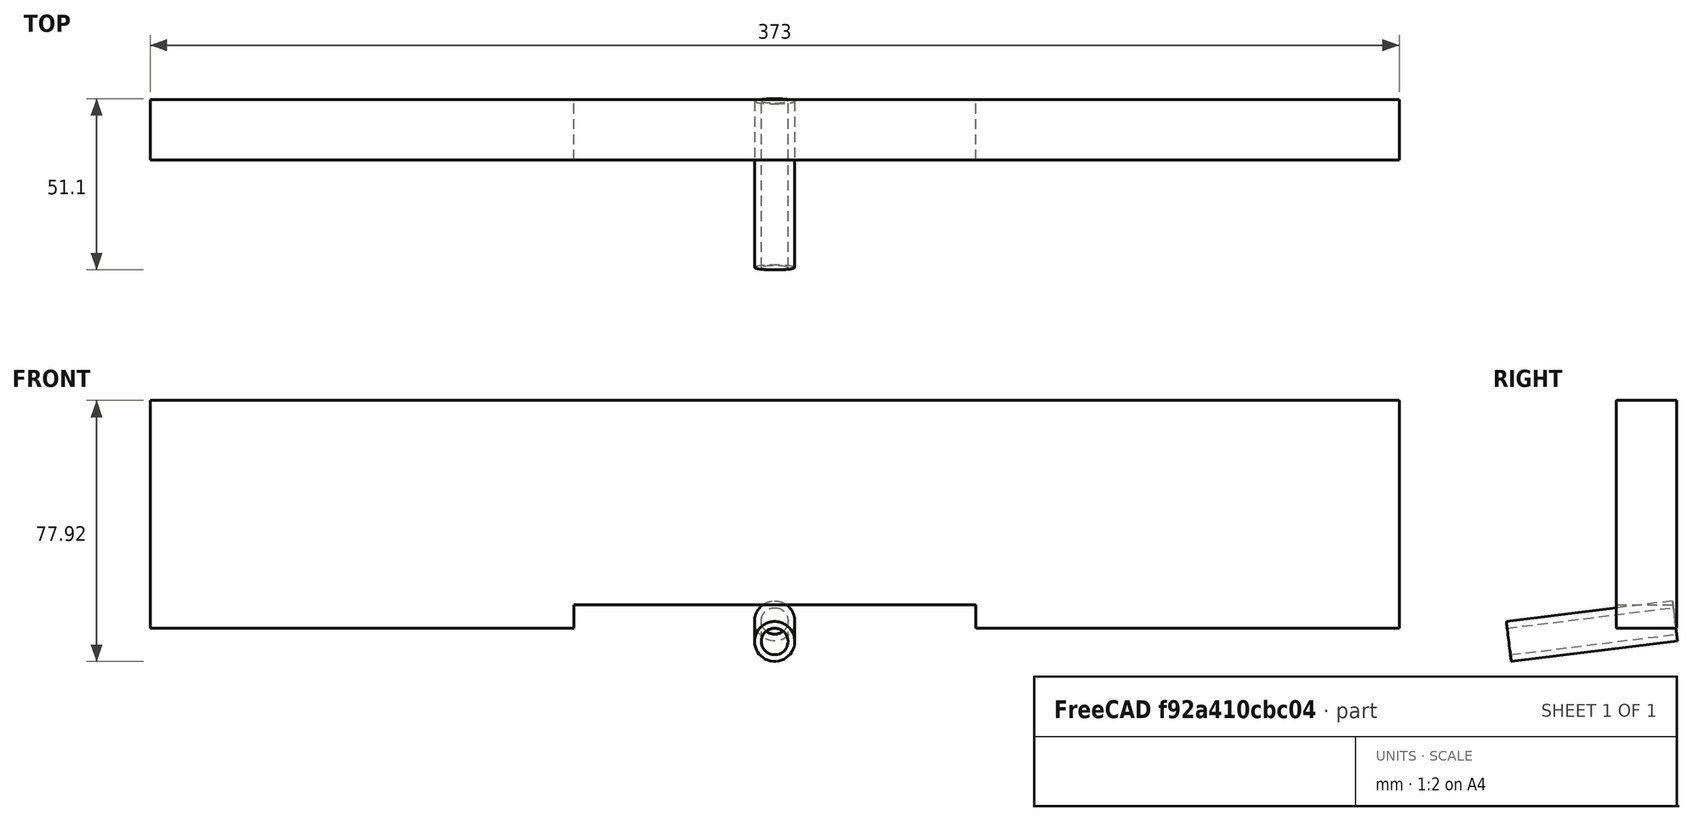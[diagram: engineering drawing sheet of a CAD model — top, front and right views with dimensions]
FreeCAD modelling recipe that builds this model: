
FCSTD DOCUMENT  (FreeCAD 0.19R)
Label: podnica_pokrovcek
License: All rights reserved
LicenseURL: http://en.wikipedia.org/wiki/All_rights_reserved
objects: App::Link×13, PartDesign::Line×12, TechDraw::DrawViewDimension×9, Sketcher::SketchObject×6, PartDesign::CoordinateSystem×6, TechDraw::DrawProjGroupItem×6, TechDraw::DrawRichAnno×5, App::Part×4, PartDesign::Body×3, App::DocumentObjectGroup×3, TechDraw::DrawProjGroup×3, PartDesign::Pad×2, TechDraw::DrawSVGTemplate×1, PartDesign::Pocket×1, App::FeaturePython×1, PartDesign::Revolution×1, TechDraw::DrawPage×1
note: 35 computed .brp shape members not serialized (recipe doc carries the construction recipe); baked Part::Feature solids carry a one-line shape summary decoded from their .brp

FEATURE [PartDesign::Body] Body
  Origin = -> Origin001
FEATURE [Sketcher::SketchObject] Sketch
  FullyConstrained = true
  MapMode = 5
  Placement = pos=(0,0,0) rot=(1,0,0;1.5708rad)
  Support = -> [XZ_Plane001]
  sketch-geometry (8):
    g0: LineSegment StartX=-186.5 StartY=0 StartZ=0 EndX=-186.5 EndY=68 EndZ=0
    g1: LineSegment StartX=-186.5 StartY=68 StartZ=0 EndX=186.5 EndY=68 EndZ=0
    g2: LineSegment StartX=186.5 StartY=68 StartZ=0 EndX=186.5 EndY=0 EndZ=0
    g3: LineSegment StartX=186.5 StartY=0 StartZ=0 EndX=60 EndY=0 EndZ=0
    g4: LineSegment StartX=60 StartY=0 StartZ=0 EndX=60 EndY=7 EndZ=0
    g5: LineSegment StartX=60 StartY=7 StartZ=0 EndX=-60 EndY=7 EndZ=0
    g6: LineSegment StartX=-60 StartY=7 StartZ=0 EndX=-60 EndY=0 EndZ=0
    g7: LineSegment StartX=-60 StartY=0 StartZ=0 EndX=-186.5 EndY=0 EndZ=0
  constraints (23):
    c: Vertical(g0)
    c: Coincident(g0,g1)
    c: Horizontal(g1)
    c: Coincident(g1,g2)
    c: Vertical(g2)
    c: Coincident(g2,g3)
    c: Horizontal(g3)
    c: Coincident(g3,g4)
    c: Vertical(g4)
    c: Coincident(g4,g5)
    c: Horizontal(g5)
    c: Coincident(g5,g6)
    c: Vertical(g6)
    c: Coincident(g6,g7)
    c: Coincident(g7,g0)
    c: Horizontal(g7)
    c: Symmetric(g6,g3,g-1)
    c: Horizontal(g6,g3)
    c: Equal(g7,g3)
    c: DistanceY(g4,g4) = 7  'H2'
    c: DistanceX(g5,g5) = 120  'L2'
    c: DistanceY(g0,g0) = 68  'H'
    c: DistanceX(g1,g1) = 373  'L'
FEATURE [PartDesign::Pad] Pad
  Direction = (1,1,1)
  Length = 18
  Length2 = 100
  Placement = pos=(0,0,0) rot=(1,0,0;1.5708rad)
  Profile = -> Sketch
  Reversed = true
  Type = 0
FEATURE [TechDraw::DrawSVGTemplate] Template
  EditableTexts = AVTOR=Brane Borštnik,AVTOR_2=Risal: Janez Paternoster,DATUM=6.5.2022,MATERIAL=Les, smreka,MERILO=1:2,NAZIV=Pokrovček v podnici,+3 more (map truncated)
  Height = 210
  Orientation = 1
  Width = 297
FEATURE [Sketcher::SketchObject] Sketch001
  FullyConstrained = true
  MapMode = 5
  Placement = pos=(0,0,0) rot=(1,0,0;1.5708rad)
  Support = -> [XZ_Plane001]
  sketch-geometry (23):
    g0: Circle CenterX=-165 CenterY=56 CenterZ=0 NormalX=0 NormalY=0 NormalZ=1 AngleXU=0 Radius=5.5
    g1: Circle CenterX=-135 CenterY=56 CenterZ=0 NormalX=0 NormalY=0 NormalZ=1 AngleXU=0 Radius=5.5
    g2: Circle CenterX=-105 CenterY=56 CenterZ=0 NormalX=0 NormalY=0 NormalZ=1 AngleXU=0 Radius=5.5
    g3: Circle CenterX=-75 CenterY=56 CenterZ=0 NormalX=0 NormalY=0 NormalZ=1 AngleXU=0 Radius=5.5
    g4: Circle CenterX=-45 CenterY=56 CenterZ=0 NormalX=0 NormalY=0 NormalZ=1 AngleXU=0 Radius=5.5
    g5: Circle CenterX=-15 CenterY=56 CenterZ=0 NormalX=0 NormalY=0 NormalZ=1 AngleXU=0 Radius=5.5
    g6: Circle CenterX=15 CenterY=56 CenterZ=0 NormalX=0 NormalY=0 NormalZ=1 AngleXU=0 Radius=5.5
    g7: Circle CenterX=45 CenterY=56 CenterZ=0 NormalX=0 NormalY=0 NormalZ=1 AngleXU=0 Radius=5.5
    g8: Circle CenterX=75 CenterY=56 CenterZ=0 NormalX=0 NormalY=0 NormalZ=1 AngleXU=0 Radius=5.5
    g9: Circle CenterX=105 CenterY=56 CenterZ=0 NormalX=0 NormalY=0 NormalZ=1 AngleXU=0 Radius=5.5
    g10: Circle CenterX=135 CenterY=56 CenterZ=0 NormalX=0 NormalY=0 NormalZ=1 AngleXU=0 Radius=5.5
    g11: Circle CenterX=165 CenterY=56 CenterZ=0 NormalX=0 NormalY=0 NormalZ=1 AngleXU=0 Radius=5.5
    g12: LineSegment StartX=-165 StartY=56 StartZ=0 EndX=-135 EndY=56 EndZ=0
    g13: LineSegment StartX=-135 StartY=56 StartZ=0 EndX=-105 EndY=56 EndZ=0
    g14: LineSegment StartX=-105 StartY=56 StartZ=0 EndX=-75 EndY=56 EndZ=0
    g15: LineSegment StartX=-75 StartY=56 StartZ=0 EndX=-45 EndY=56 EndZ=0
    g16: LineSegment StartX=-45 StartY=56 StartZ=0 EndX=-15 EndY=56 EndZ=0
    g17: LineSegment StartX=-15 StartY=56 StartZ=0 EndX=15 EndY=56 EndZ=0
    g18: LineSegment StartX=15 StartY=56 StartZ=0 EndX=45 EndY=56 EndZ=0
    g19: LineSegment StartX=45 StartY=56 StartZ=0 EndX=75 EndY=56 EndZ=0
    g20: LineSegment StartX=75 StartY=56 StartZ=0 EndX=105 EndY=56 EndZ=0
    g21: LineSegment StartX=105 StartY=56 StartZ=0 EndX=135 EndY=56 EndZ=0
    g22: LineSegment StartX=135 StartY=56 StartZ=0 EndX=165 EndY=56 EndZ=0
  constraints (50):
    c: Horizontal(g12)
    c: Coincident(g12,g13)
    c: Horizontal(g13)
    c: Coincident(g13,g14)
    c: Horizontal(g14)
    c: Coincident(g14,g15)
    c: Coincident(g15,g16)
    c: Horizontal(g16)
    c: Coincident(g16,g17)
    c: Coincident(g17,g18)
    c: Horizontal(g18)
    c: Coincident(g18,g19)
    c: Horizontal(g19)
    c: Coincident(g19,g20)
    c: Horizontal(g20)
    c: Coincident(g20,g21)
    c: Horizontal(g21)
    c: Coincident(g21,g22)
    c: Horizontal(g22)
    c: Horizontal(g15)
    c: Symmetric(g16,g17,g-2)
    c: Equal(g17,g16)
    c: Equal(g17,g15)
    c: Equal(g17,g14)
    c: Equal(g17,g13)
    c: Equal(g17,g12)
    c: Equal(g17, g18-g22) x5
    c: Coincident(g0,g12)
    c: Coincident(g1,g12)
    c: Coincident(g2,g13)
    c: Coincident(g3,g14)
    c: Coincident(g4,g15)
    c: Coincident(g5,g16)
    c: Coincident(g6,g17)
    c: Coincident(g18,g7)
    c: Coincident(g8,g19)
    c: Coincident(g9,g20)
    c: Coincident(g22,g11)
    c: Coincident(g10,g21)
    c: Equal(g5,g4)
    c: Equal(g5,g3)
    c: Equal(g5,g2)
    c: Equal(g5,g1)
    c: Equal(g5,g0)
    c: Equal(g5,g6)
    c: Equal(g6, g7-g11) x5
    c: Diameter(g0) = 11
    c: DistanceX(g17,g17) = 30
    c: DistanceX(g0,g11) = 330
    c: DistanceY(g-1,g0) = 56
FEATURE [PartDesign::Pocket] Pocket
  BaseFeature = -> Pad
  Length = 5
  Length2 = 100
  Placement = pos=(0,0,0) rot=(1,0,0;1.5708rad)
  Profile = -> Sketch001
  Type = 1
FEATURE [PartDesign::CoordinateSystem] LCS_Origin
  AttacherType = Attacher::AttachEngine3D
  MapMode = 2
  Support = -> [X_Axis002]
FEATURE [App::FeaturePython] Variables  # WARN: FeaturePython — macro-defined, semantics opaque (R4)
  Type = App::PropertyContainer
FEATURE [App::DocumentObjectGroup] Constraints
FEATURE [App::DocumentObjectGroup] Configurations
FEATURE [PartDesign::CoordinateSystem] LCS_0
  AttacherType = Attacher::AttachEngine3D
  MapMode = 2
  Support = -> [X_Axis003]
FEATURE [PartDesign::CoordinateSystem] LCS_0001
  AttacherType = Attacher::AttachEngine3D
  MapMode = 2
  Support = -> [X_Axis004]
FEATURE [Sketcher::SketchObject] Sketch004
  FullyConstrained = true
  MapMode = 5
  Placement = pos=(0,0,0) rot=(1,0,0;1.5708rad)
  Support = -> [XZ_Plane004]
  expr: Constraints[18] = Sketch.Constraints.L
  expr: Constraints[19] = Sketch.Constraints.H
  expr: Constraints[20] = Sketch.Constraints.L2
  expr: Constraints[21] = Sketch.Constraints.H2
  sketch-geometry (8):
    g0: LineSegment StartX=-186.5 StartY=68 StartZ=0 EndX=186.5 EndY=68 EndZ=0
    g1: LineSegment StartX=186.5 StartY=68 StartZ=0 EndX=186.5 EndY=0 EndZ=0
    g2: LineSegment StartX=186.5 StartY=0 StartZ=0 EndX=60 EndY=0 EndZ=0
    g3: LineSegment StartX=60 StartY=0 StartZ=0 EndX=60 EndY=7 EndZ=0
    g4: LineSegment StartX=60 StartY=7 StartZ=0 EndX=-60 EndY=7 EndZ=0
    g5: LineSegment StartX=-60 StartY=7 StartZ=0 EndX=-60 EndY=0 EndZ=0
    g6: LineSegment StartX=-60 StartY=0 StartZ=0 EndX=-186.5 EndY=0 EndZ=0
    g7: LineSegment StartX=-186.5 StartY=0 StartZ=0 EndX=-186.5 EndY=68 EndZ=0
  constraints (23):
    c: Horizontal(g0)
    c: Coincident(g0,g1)
    c: Vertical(g1)
    c: Coincident(g1,g2)
    c: Horizontal(g2)
    c: Coincident(g2,g3)
    c: Vertical(g3)
    c: Coincident(g3,g4)
    c: Horizontal(g4)
    c: Coincident(g4,g5)
    c: Vertical(g5)
    c: Coincident(g5,g6)
    c: Horizontal(g6)
    c: Coincident(g6,g7)
    c: Coincident(g7,g0)
    c: Vertical(g7)
    c: Horizontal(g5,g2)
    c: Symmetric(g2,g5,g-1)
    c: DistanceX(g0,g0) = 373
    c: DistanceY(g7,g7) = 68
    c: DistanceX(g4,g4) = 120
    c: DistanceY(g5,g5) = 7
    c: Equal(g6,g2)
FEATURE [PartDesign::Pad] Pad001
  Direction = (1,1,1)
  Length = 18
  Length2 = 100
  Placement = pos=(0,0,0) rot=(1,0,0;1.5708rad)
  Profile = -> Sketch004
  Reversed = true
  Type = 0
  expr: Length = Pad.Length
FEATURE [Sketcher::SketchObject] Sketch005
  FullyConstrained = true
  MapMode = 5
  Placement = pos=(0,0,0) rot=(0.57735,0.57735,0.57735;2.0944rad)
  Support = -> [YZ_Plane004]
  sketch-geometry (4):
    g0: LineSegment StartX=-32.6227 StartY=0 StartZ=0 EndX=17 EndY=6.1307 EndZ=0
    g1: LineSegment StartX=17 StartY=6.1307 StartZ=0 EndX=16.7548 EndY=8.11561 EndZ=0
    g2: LineSegment StartX=16.7548 StartY=8.11561 StartZ=0 EndX=-32.868 EndY=1.98491 EndZ=0
    g3: LineSegment StartX=-32.868 StartY=1.98491 StartZ=0 EndX=-32.6227 EndY=0 EndZ=0
  constraints (12):
    c: Coincident(g0,g1)
    c: Coincident(g1,g2)
    c: Coincident(g2,g3)
    c: Coincident(g3,g0)
    c: Perpendicular(g1,g0)
    c: Perpendicular(g2,g1)
    c: Perpendicular(g3,g2)
    c: Distance(g-1,g0) = 4
    c: Distance(g-1,g2) = 6
    c: DistanceX(g-1,g0) = 17
    c: Distance(g2) = 50
    c: Horizontal(g0,g-1)
FEATURE [PartDesign::Body] Body_2
  Group = -> [LCS_0001,Sketch004,Pad001,Sketch005]
  Origin = -> Origin004
  Tip = -> Pad001
FEATURE [App::Part] pokrovcek_navaden
  Group = -> [LCS_0,Body_2]
  Origin = -> Origin003
FEATURE [PartDesign::CoordinateSystem] LCS_0002
  AttacherType = Attacher::AttachEngine3D
  MapMode = 2
  Support = -> [X_Axis005]
FEATURE [PartDesign::CoordinateSystem] LCS_0003
  AttacherType = Attacher::AttachEngine3D
  MapMode = 2
  Support = -> [X_Axis006]
FEATURE [Sketcher::SketchObject] Sketch006
  FullyConstrained = true
  MapMode = 5
  Placement = pos=(0,0,0) rot=(0.57735,0.57735,0.57735;2.0944rad)
  Support = -> [YZ_Plane006]
  sketch-geometry (5):
    g0: LineSegment StartX=-32.6227 StartY=0 StartZ=0 EndX=17 EndY=6.1307 EndZ=0
    g1: LineSegment StartX=17 StartY=6.1307 StartZ=0 EndX=16.7548 EndY=8.11561 EndZ=0
    g2: LineSegment StartX=16.7548 StartY=8.11561 StartZ=0 EndX=-32.868 EndY=1.98491 EndZ=0
    g3: LineSegment StartX=-32.868 StartY=1.98491 StartZ=0 EndX=-32.6227 EndY=0 EndZ=0
    g4: LineSegment StartX=-32.6227 StartY=-4.03041 StartZ=0 EndX=17 EndY=2.10028 EndZ=0
  constraints (16):
    c: Coincident(g0,g1)
    c: Coincident(g1,g2)
    c: Coincident(g2,g3)
    c: Coincident(g3,g0)
    c: Perpendicular(g1,g0)
    c: Perpendicular(g2,g1)
    c: Perpendicular(g3,g2)
    c: Distance(g-1,g0) = 4
    c: Distance(g-1,g2) = 6
    c: DistanceX(g-1,g0) = 17
    c: Distance(g2) = 50
    c: Horizontal(g0,g-1)
    c: PointOnObject(g-1,g4)
    c: Parallel(g4,g0)
    c: Vertical(g0,g4)
    c: Vertical(g0,g4)
FEATURE [PartDesign::Revolution] Revolution
  Angle = 360
  Axis = (1.52e-14,49.6227,6.1307)
  Base = (-1e-14,-32.6227,-4.03041)
  Placement = pos=(0,0,0) rot=(0.57735,0.57735,0.57735;2.0944rad)
  Profile = -> Sketch006
  ReferenceAxis = -> Sketch006 [Axis0]
FEATURE [App::Link] pokrovcek_smukalnik  label="pokrovcek_smukalnik001"
  AssemblyType = Part::Link
  LinkedObject = -> Part
FEATURE [PartDesign::CoordinateSystem] LCS_1
  AttacherType = Attacher::AttachEngine3D
FEATURE [PartDesign::Line] HoleAxis_1
  AttacherType = Attacher::AttachEngineLine
  Length = 15.4997
  MapMode = 19
  Placement = pos=(-165,1.24e-14,56) rot=(1,0,0;1.5708rad)
  ResizeMode = 1
  Support = -> [Pocket]
FEATURE [App::Link] cevka002  label="cevka1"
  AssemblyType = Part::Link
  AttachedBy = #LCS_0002
  AttachedTo = pokrovcek_smukalnik#HoleAxis_1
  AttachmentOffset = pos=(0,0,0) rot=(1,0,0;4.71239rad)
  LinkPlacement = pos=(-165,3.73e-14,56) rot=(0,0,1;0rad)
  LinkedObject = -> cevka
  Placement = pos=(-165,3.73e-14,56) rot=(0,0,1;0rad)
  SolverId = Asm4EE
  expr: Placement = pokrovcek_smukalnik.Placement * HoleAxis_1.Placement * AttachmentOffset * LCS_0002.Placement ^ -1
FEATURE [PartDesign::Line] HoleAxis_2 .. HoleAxis_12  x11 (patterned run collapsed; names and placements below)
  AttacherType = Attacher::AttachEngineLine
  Length = 15.4997
  MapMode = 19
  ResizeMode = 1
  Support = -> [Pocket]
  placements: 11 in arithmetic series — first pos=(-135,1.24e-14,56) rot=(1,0,0;1.5708rad), step (30,0,0), last pos=(165,1.24e-14,56) rot=(1,0,0;1.5708rad)
FEATURE [App::Part] Part  label="pokrovcek_smukalnik"
  Group = -> [Body,LCS_1,Sketch001,Pocket,Pad,Sketch,HoleAxis_1,HoleAxis_2,HoleAxis_3,HoleAxis_4,HoleAxis_5,HoleAxis_6,HoleAxis_7,HoleAxis_8,HoleAxis_9,HoleAxis_10,HoleAxis_11,HoleAxis_12]
  Origin = -> Origin
FEATURE [TechDraw::DrawProjGroupItem] ProjItem  label="Front"
  CoarseView = false
  Direction = (0,-1,0)
  Focus = 100
  HardHidden = false
  IsoCount = 0
  IsoHidden = false
  IsoVisible = false
  LockPosition = true
  Perspective = false
  Rotation = 0
  RotationVector = (1,0,0)
  Scale = 0.5
  ScaleType = 2
  SeamHidden = false
  SeamVisible = true
  SmoothHidden = false
  SmoothVisible = true
  Source = -> [Part]
  Type = 0
  X = 0
  XDirection = (1,0,0)
  Y = 0
FEATURE [TechDraw::DrawProjGroupItem] ProjItem001  label="Left"
  CoarseView = false
  Direction = (-1,-1e-16,0)
  Focus = 100
  HardHidden = false
  IsoCount = 0
  IsoHidden = false
  IsoVisible = false
  LockPosition = false
  Perspective = false
  Rotation = 0
  RotationVector = (1,0,0)
  Scale = 0.5
  ScaleType = 2
  SeamHidden = false
  SeamVisible = true
  SmoothHidden = false
  SmoothVisible = true
  Source = -> [Part]
  Type = 1
  X = 127.75
  XDirection = (1e-16,-1,0)
  Y = 0
FEATURE [TechDraw::DrawProjGroup] ProjGroup
  Anchor = -> ProjItem
  AutoDistribute = true
  LockPosition = false
  ProjectionType = 0
  Rotation = 0
  Scale = 0.5
  ScaleType = 0
  Source = -> [Part]
  Views = -> [ProjItem,ProjItem001]
  X = 113.771
  Y = 141.789
  spacingX = 30
  spacingY = 15
FEATURE [TechDraw::DrawViewDimension] Dimension
  Arbitrary = false
  ArbitraryTolerances = false
  EqualTolerance = true
  FormatSpec = %.6g
  FormatSpecOverTolerance = %+.6g
  FormatSpecUnderTolerance = %+.6g
  Inverted = false
  LockPosition = false
  MeasureType = 1
  OverTolerance = 0
  References2D = -> [ProjItem001]
  Rotation = 0
  Scale = 0.5
  ScaleType = 0
  TheoreticalExact = false
  Type = 1
  UnderTolerance = 0
  X = -0.601719
  Y = 39.2636
FEATURE [TechDraw::DrawViewDimension] Dimension001
  Arbitrary = false
  ArbitraryTolerances = false
  EqualTolerance = true
  FormatSpec = %.6g
  FormatSpecOverTolerance = %+.6g
  FormatSpecUnderTolerance = %+.6g
  Inverted = false
  LockPosition = false
  MeasureType = 1
  OverTolerance = 0
  References2D = -> [ProjItem001]
  Rotation = 0
  Scale = 0.5
  ScaleType = 0
  TheoreticalExact = false
  Type = 2
  UnderTolerance = 0
  X = 16.2335
  Y = 1.80516
FEATURE [TechDraw::DrawViewDimension] Dimension002
  Arbitrary = false
  ArbitraryTolerances = false
  EqualTolerance = true
  FormatSpec = %.6g
  FormatSpecOverTolerance = %+.6g
  FormatSpecUnderTolerance = %+.6g
  Inverted = false
  LockPosition = false
  MeasureType = 1
  OverTolerance = 0
  References2D = -> [ProjItem]
  Rotation = 0
  Scale = 0.5
  ScaleType = 0
  TheoreticalExact = false
  Type = 1
  UnderTolerance = 0
  X = 0.902579
  Y = 42.5731
FEATURE [TechDraw::DrawViewDimension] Dimension003
  Arbitrary = false
  ArbitraryTolerances = false
  EqualTolerance = true
  FormatSpec = %.6g
  FormatSpecOverTolerance = %+.6g
  FormatSpecUnderTolerance = %+.6g
  Inverted = false
  LockPosition = false
  MeasureType = 1
  OverTolerance = 0
  References2D = -> [ProjItem]
  Rotation = 0
  Scale = 0.5
  ScaleType = 0
  TheoreticalExact = false
  Type = 1
  UnderTolerance = 0
  X = -2.10602
  Y = -25.8352
FEATURE [TechDraw::DrawViewDimension] Dimension004
  Arbitrary = false
  ArbitraryTolerances = false
  EqualTolerance = true
  FormatSpec = %.6g
  FormatSpecOverTolerance = %+.6g
  FormatSpecUnderTolerance = %+.6g
  Inverted = false
  LockPosition = false
  MeasureType = 1
  OverTolerance = 0
  References2D = -> [ProjItem]
  Rotation = 0
  Scale = 0.5
  ScaleType = 0
  TheoreticalExact = false
  Type = 2
  UnderTolerance = 0
  X = -36.6189
  Y = -27.5852
FEATURE [TechDraw::DrawViewDimension] Dimension005
  Arbitrary = false
  ArbitraryTolerances = false
  EqualTolerance = true
  FormatSpec = %.6g
  FormatSpecOverTolerance = %+.6g
  FormatSpecUnderTolerance = %+.6g
  Inverted = false
  LockPosition = false
  MeasureType = 1
  OverTolerance = 0
  References2D = -> [ProjItem]
  Rotation = 0
  Scale = 0.5
  ScaleType = 0
  TheoreticalExact = false
  Type = 1
  UnderTolerance = 0
  X = -0.30086
  Y = 34.1662
FEATURE [TechDraw::DrawViewDimension] Dimension006
  Arbitrary = false
  ArbitraryTolerances = false
  EqualTolerance = true
  FormatSpec = ⌀%.6g, 12x
  FormatSpecOverTolerance = %+.6g
  FormatSpecUnderTolerance = %+.6g
  Inverted = false
  LockPosition = false
  MeasureType = 1
  OverTolerance = 0
  References2D = -> [ProjItem]
  Rotation = 0
  Scale = 0.5
  ScaleType = 0
  TheoreticalExact = false
  Type = 5
  UnderTolerance = 0
  X = -75.5158
  Y = 28.5817
FEATURE [App::Link] cevka003
  AssemblyType = Part::Link
  AttachedBy = #LCS_0002
  AttachedTo = pokrovcek_smukalnik#HoleAxis_2
  AttachmentOffset = pos=(0,0,0) rot=(1,0,0;4.71239rad)
  LinkPlacement = pos=(-135,3.73e-14,56) rot=(0,0,1;0rad)
  LinkedObject = -> cevka
  Placement = pos=(-135,3.73e-14,56) rot=(0,0,1;0rad)
  SolverId = Asm4EE
  expr: Placement = pokrovcek_smukalnik.Placement * HoleAxis_2.Placement * AttachmentOffset * LCS_0002.Placement ^ -1
FEATURE [App::Link] cevka_2
  AssemblyType = Part::Link
  AttachedBy = #LCS_0002
  AttachedTo = pokrovcek_smukalnik#HoleAxis_3
  AttachmentOffset = pos=(0,0,0) rot=(1,0,0;4.71239rad)
  LinkPlacement = pos=(-105,3.73e-14,56) rot=(0,0,1;0rad)
  LinkedObject = -> cevka
  Placement = pos=(-105,3.73e-14,56) rot=(0,0,1;0rad)
  SolverId = Asm4EE
  expr: Placement = pokrovcek_smukalnik.Placement * HoleAxis_3.Placement * AttachmentOffset * LCS_0002.Placement ^ -1
FEATURE [App::Link] cevka_3
  AssemblyType = Part::Link
  AttachedBy = #LCS_0002
  AttachedTo = pokrovcek_smukalnik#HoleAxis_4
  AttachmentOffset = pos=(0,0,0) rot=(1,0,0;4.71239rad)
  LinkPlacement = pos=(-75,3.73e-14,56) rot=(0,0,1;0rad)
  LinkedObject = -> cevka
  Placement = pos=(-75,3.73e-14,56) rot=(0,0,1;0rad)
  SolverId = Asm4EE
  expr: Placement = pokrovcek_smukalnik.Placement * HoleAxis_4.Placement * AttachmentOffset * LCS_0002.Placement ^ -1
FEATURE [App::Link] cevka_4
  AssemblyType = Part::Link
  AttachedBy = #LCS_0002
  AttachedTo = pokrovcek_smukalnik#HoleAxis_5
  AttachmentOffset = pos=(0,0,0) rot=(1,0,0;4.71239rad)
  LinkPlacement = pos=(-45,3.73e-14,56) rot=(0,0,1;0rad)
  LinkedObject = -> cevka
  Placement = pos=(-45,3.73e-14,56) rot=(0,0,1;0rad)
  SolverId = Asm4EE
  expr: Placement = pokrovcek_smukalnik.Placement * HoleAxis_5.Placement * AttachmentOffset * LCS_0002.Placement ^ -1
FEATURE [App::Link] cevka_5
  AssemblyType = Part::Link
  AttachedBy = #LCS_0002
  AttachedTo = pokrovcek_smukalnik#HoleAxis_6
  AttachmentOffset = pos=(0,0,0) rot=(1,0,0;4.71239rad)
  LinkPlacement = pos=(-15,3.73e-14,56) rot=(0,0,1;0rad)
  LinkedObject = -> cevka
  Placement = pos=(-15,3.73e-14,56) rot=(0,0,1;0rad)
  SolverId = Asm4EE
  expr: Placement = pokrovcek_smukalnik.Placement * HoleAxis_6.Placement * AttachmentOffset * LCS_0002.Placement ^ -1
FEATURE [App::Link] cevka_6
  AssemblyType = Part::Link
  AttachedBy = #LCS_0002
  AttachedTo = pokrovcek_smukalnik#HoleAxis_7
  AttachmentOffset = pos=(0,0,0) rot=(1,0,0;4.71239rad)
  LinkPlacement = pos=(15,3.73e-14,56) rot=(0,0,1;0rad)
  LinkedObject = -> cevka
  Placement = pos=(15,3.73e-14,56) rot=(0,0,1;0rad)
  SolverId = Asm4EE
  expr: Placement = pokrovcek_smukalnik.Placement * HoleAxis_7.Placement * AttachmentOffset * LCS_0002.Placement ^ -1
FEATURE [App::Link] cevka_7
  AssemblyType = Part::Link
  AttachedBy = #LCS_0002
  AttachedTo = pokrovcek_smukalnik#HoleAxis_8
  AttachmentOffset = pos=(0,0,0) rot=(1,0,0;4.71239rad)
  LinkPlacement = pos=(45,3.73e-14,56) rot=(0,0,1;0rad)
  LinkedObject = -> cevka
  Placement = pos=(45,3.73e-14,56) rot=(0,0,1;0rad)
  SolverId = Asm4EE
  expr: Placement = pokrovcek_smukalnik.Placement * HoleAxis_8.Placement * AttachmentOffset * LCS_0002.Placement ^ -1
FEATURE [App::Link] cevka_8
  AssemblyType = Part::Link
  AttachedBy = #LCS_0002
  AttachedTo = pokrovcek_smukalnik#HoleAxis_9
  AttachmentOffset = pos=(0,0,0) rot=(1,0,0;4.71239rad)
  LinkPlacement = pos=(75,3.73e-14,56) rot=(0,0,1;0rad)
  LinkedObject = -> cevka
  Placement = pos=(75,3.73e-14,56) rot=(0,0,1;0rad)
  SolverId = Asm4EE
  expr: Placement = pokrovcek_smukalnik.Placement * HoleAxis_9.Placement * AttachmentOffset * LCS_0002.Placement ^ -1
FEATURE [App::Link] cevka_9
  AssemblyType = Part::Link
  AttachedBy = #LCS_0002
  AttachedTo = pokrovcek_smukalnik#HoleAxis_10
  AttachmentOffset = pos=(0,0,0) rot=(1,0,0;4.71239rad)
  LinkPlacement = pos=(105,3.73e-14,56) rot=(0,0,1;0rad)
  LinkedObject = -> cevka
  Placement = pos=(105,3.73e-14,56) rot=(0,0,1;0rad)
  SolverId = Asm4EE
  expr: Placement = pokrovcek_smukalnik.Placement * HoleAxis_10.Placement * AttachmentOffset * LCS_0002.Placement ^ -1
FEATURE [App::Link] cevka_10
  AssemblyType = Part::Link
  AttachedBy = #LCS_0002
  AttachedTo = pokrovcek_smukalnik#HoleAxis_11
  AttachmentOffset = pos=(0,0,0) rot=(1,0,0;4.71239rad)
  LinkPlacement = pos=(135,3.73e-14,56) rot=(0,0,1;0rad)
  LinkedObject = -> cevka
  Placement = pos=(135,3.73e-14,56) rot=(0,0,1;0rad)
  SolverId = Asm4EE
  expr: Placement = pokrovcek_smukalnik.Placement * HoleAxis_11.Placement * AttachmentOffset * LCS_0002.Placement ^ -1
FEATURE [App::Link] cevka_11
  AssemblyType = Part::Link
  AttachedBy = #LCS_0002
  AttachedTo = pokrovcek_smukalnik#HoleAxis_12
  AttachmentOffset = pos=(0,0,0) rot=(1,0,0;4.71239rad)
  LinkPlacement = pos=(165,3.73e-14,56) rot=(0,0,1;0rad)
  LinkedObject = -> cevka
  Placement = pos=(165,3.73e-14,56) rot=(0,0,1;0rad)
  SolverId = Asm4EE
  expr: Placement = pokrovcek_smukalnik.Placement * HoleAxis_12.Placement * AttachmentOffset * LCS_0002.Placement ^ -1
FEATURE [App::Part] Assembly
  AssemblyType = Part::Link
  Group = -> [LCS_Origin,Variables,Constraints,Configurations,pokrovcek_smukalnik,cevka002,cevka003,cevka_2,cevka_3,cevka_4,cevka_5,cevka_6,cevka_7,cevka_8,cevka_9,cevka_10,cevka_11]
  Origin = -> Origin002
  Type = Assembly
FEATURE [TechDraw::DrawProjGroupItem] ProjItem002  label="Front001"
  CoarseView = false
  Direction = (0,-1,0)
  Focus = 100
  HardHidden = false
  IsoCount = 0
  IsoHidden = false
  IsoVisible = false
  LockPosition = true
  Perspective = false
  Rotation = 0
  RotationVector = (1,0,0)
  ScaleType = 2
  SeamHidden = false
  SeamVisible = true
  SmoothHidden = false
  SmoothVisible = true
  Source = -> [pokrovcek_navaden]
  Type = 0
  X = 0
  XDirection = (1,0,0)
  Y = 0
FEATURE [TechDraw::DrawProjGroupItem] ProjItem003  label="Left001"
  CoarseView = false
  Direction = (-1,-1e-16,0)
  Focus = 100
  HardHidden = false
  IsoCount = 0
  IsoHidden = false
  IsoVisible = false
  LockPosition = false
  Perspective = false
  Rotation = 0
  RotationVector = (1,0,0)
  ScaleType = 2
  SeamHidden = false
  SeamVisible = true
  SmoothHidden = false
  SmoothVisible = true
  Source = -> [pokrovcek_navaden]
  Type = 1
  X = 112.75
  XDirection = (1e-16,-1,0)
  Y = 0
FEATURE [TechDraw::DrawProjGroup] ProjGroup001
  Anchor = -> ProjItem002
  AutoDistribute = true
  LockPosition = false
  ProjectionType = 0
  Rotation = 0
  Scale = 0.5
  ScaleType = 0
  Source = -> [pokrovcek_navaden]
  Views = -> [ProjItem002,ProjItem003]
  X = 114.804
  Y = 54.1547
  spacingX = 15
  spacingY = 15
FEATURE [Sketcher::SketchObject] Sketch007
  FullyConstrained = true
  MapMode = 5
  Placement = pos=(-9.1e-15,-32.1323,-3.96982) rot=(0.599592,0.599592,-0.530074;2.16676rad)
  Support = -> [Revolution]
FEATURE [PartDesign::Body] Body_3
  Group = -> [LCS_0003,Sketch006,Revolution,Sketch007]
  Origin = -> Origin006
  Tip = -> Revolution
FEATURE [App::Part] cevka
  Group = -> [LCS_0002,Body_3]
  Origin = -> Origin005
FEATURE [App::DocumentObjectGroup] Parts
  Group = -> [Part,pokrovcek_navaden,cevka]
FEATURE [TechDraw::DrawProjGroupItem] ProjItem007  label="Front004"
  CoarseView = false
  Direction = (0.997,-0.013,0.071)
  Focus = 100
  HardHidden = false
  IsoCount = 0
  IsoHidden = false
  IsoVisible = false
  LockPosition = true
  Perspective = false
  Rotation = 0
  RotationVector = (0.004,0.992,0.126)
  ScaleType = 2
  SeamHidden = false
  SeamVisible = true
  SmoothHidden = false
  SmoothVisible = true
  Source = -> [cevka]
  Type = 0
  X = 0
  XDirection = (0.004,0.992,0.126)
  Y = 0
FEATURE [TechDraw::DrawProjGroupItem] ProjItem008  label="Left002"
  CoarseView = false
  Direction = (-0.00396217,-0.992022,-0.126)
  Focus = 100
  HardHidden = false
  IsoCount = 0
  IsoHidden = false
  IsoVisible = false
  LockPosition = false
  Perspective = false
  Rotation = 0
  RotationVector = (1,0,0)
  ScaleType = 2
  SeamHidden = false
  SeamVisible = true
  SmoothHidden = false
  SmoothVisible = true
  Source = -> [cevka]
  Type = 1
  X = 30.568
  XDirection = (0.99739,-0.0130051,0.0710277)
  Y = 0
FEATURE [TechDraw::DrawProjGroup] ProjGroup004
  Anchor = -> ProjItem007
  AutoDistribute = true
  LockPosition = false
  ProjectionType = 0
  Rotation = 0
  Scale = 0.5
  ScaleType = 0
  Source = -> [cevka]
  Views = -> [ProjItem007,ProjItem008]
  X = 212.552
  Y = 95.1458
  spacingX = 15
  spacingY = 15
FEATURE [TechDraw::DrawViewDimension] Dimension009
  Arbitrary = false
  ArbitraryTolerances = false
  EqualTolerance = true
  FormatSpec = %.0f
  FormatSpecOverTolerance = %+.6g
  FormatSpecUnderTolerance = %+.6g
  Inverted = false
  LockPosition = false
  MeasureType = 1
  OverTolerance = 0
  References2D = -> [ProjItem007]
  Rotation = 0
  Scale = 0.5
  ScaleType = 0
  TheoreticalExact = false
  Type = 1
  UnderTolerance = 0
  X = 0.645995
  Y = 15.0715
FEATURE [TechDraw::DrawViewDimension] Dimension010
  Arbitrary = false
  ArbitraryTolerances = false
  EqualTolerance = true
  FormatSpec = ⌀%.0f
  FormatSpecOverTolerance = %+.6g
  FormatSpecUnderTolerance = %+.6g
  Inverted = false
  LockPosition = false
  MeasureType = 1
  OverTolerance = 0
  References2D = -> [ProjItem008]
  Rotation = 0
  Scale = 0.5
  ScaleType = 0
  TheoreticalExact = false
  Type = 5
  UnderTolerance = 0
  X = 13.033
  Y = 14.9402
FEATURE [TechDraw::DrawRichAnno] RichTextAnnotation
  AnnoParent = -> ProjItem007
  AnnoText = <!DOCTYPE HTML PUBLIC "-//W3C//DTD HTML 4.0//EN" "http://www.w3.org/TR/REC-html40/strict.dtd">\n<html><head><meta name="qrichtext" content="1" /><style type="text/css">\np, li { white-space: pre-wrap; }\n</style></head><body style=" font-family:'Ubuntu'; font-size:11pt; font-weight:400; font-style:normal;">\n<p style=" margin-top:0px; margin-bottom:0px; margin-left:0px; margin-right:0px; -qt-block-indent:0; text-indent:0px;"><span style=" font-size:10pt;">Cevke, 12 kom</span></p></body></html>
  LockPosition = false
  MaxWidth = -1
  Rotation = 0
  Scale = 0.5
  ScaleType = 0
  ShowFrame = false
  X = 19.8673
  Y = -10.8078
FEATURE [TechDraw::DrawRichAnno] RichTextAnnotation001
  AnnoParent = -> ProjItem
  AnnoText = <!DOCTYPE HTML PUBLIC "-//W3C//DTD HTML 4.0//EN" "http://www.w3.org/TR/REC-html40/strict.dtd">\n<html><head><meta name="qrichtext" content="1" /><style type="text/css">\np, li { white-space: pre-wrap; }\n</style></head><body style=" font-family:'Ubuntu'; font-size:11pt; font-weight:400; font-style:normal;">\n<p style=" margin-top:0px; margin-bottom:0px; margin-left:0px; margin-right:0px; -qt-block-indent:0; text-indent:0px;"><span style=" font-size:10pt;">Pokrovček za smukalnik.</span></p>\n<p style=" margin-top:0px; margin-bottom:0px; margin-left:0px; margin-right:0px; -qt-block-indent:0; text-indent:0px;"><span style=" font-size:10pt;">V luknje se vstavijo cevke,</span></p>\n<p style=" margin-top:0px; margin-bottom:0px; margin-left:0px; margin-right:0px; -qt-block-indent:0; text-indent:0px;"><span style=" font-size:10pt;">ki naj bodo obrnjene rahlo navzdol</span></p></body></html>
  LockPosition = false
  MaxWidth = -1
  Rotation = 0
  Scale = 0.5
  ScaleType = 0
  ShowFrame = false
  X = 49.9067
  Y = -3.81453
FEATURE [TechDraw::DrawRichAnno] RichTextAnnotation002
  AnnoParent = -> ProjItem002
  AnnoText = <!DOCTYPE HTML PUBLIC "-//W3C//DTD HTML 4.0//EN" "http://www.w3.org/TR/REC-html40/strict.dtd">\n<html><head><meta name="qrichtext" content="1" /><style type="text/css">\np, li { white-space: pre-wrap; }\n</style></head><body style=" font-family:'Ubuntu'; font-size:11pt; font-weight:400; font-style:normal;">\n<p style=" margin-top:0px; margin-bottom:0px; margin-left:0px; margin-right:0px; -qt-block-indent:0; text-indent:0px;"><span style=" font-size:10pt;">Navaden pokrovček na podnici</span></p></body></html>
  LockPosition = false
  MaxWidth = -1
  Rotation = 0
  Scale = 0.5
  ScaleType = 0
  ShowFrame = false
  X = 0
  Y = 0
FEATURE [TechDraw::DrawRichAnno] RichTextAnnotation003
  AnnoParent = -> ProjItem
  AnnoText = <!DOCTYPE HTML PUBLIC "-//W3C//DTD HTML 4.0//EN" "http://www.w3.org/TR/REC-html40/strict.dtd">\n<html><head><meta name="qrichtext" content="1" /><style type="text/css">\np, li { white-space: pre-wrap; }\n</style></head><body style=" font-family:'Ubuntu'; font-size:11pt; font-weight:400; font-style:normal;">\n<p style=" margin-top:0px; margin-bottom:0px; margin-left:0px; margin-right:0px; -qt-block-indent:0; text-indent:0px;"><span style=" font-size:10pt;">1 kom</span></p></body></html>
  LockPosition = false
  MaxWidth = -1
  Rotation = 0
  Scale = 0.5
  ScaleType = 0
  ShowFrame = false
  X = -76.7192
  Y = -6.01719
FEATURE [TechDraw::DrawRichAnno] RichTextAnnotation004
  AnnoParent = -> ProjItem002
  AnnoText = <!DOCTYPE HTML PUBLIC "-//W3C//DTD HTML 4.0//EN" "http://www.w3.org/TR/REC-html40/strict.dtd">\n<html><head><meta name="qrichtext" content="1" /><style type="text/css">\np, li { white-space: pre-wrap; }\n</style></head><body style=" font-family:'Ubuntu'; font-size:11pt; font-weight:400; font-style:normal;">\n<p style=" margin-top:0px; margin-bottom:0px; margin-left:0px; margin-right:0px; -qt-block-indent:0; text-indent:0px;"><span style=" font-size:10pt;">1 kom</span></p></body></html>
  LockPosition = false
  MaxWidth = -1
  Rotation = 0
  Scale = 0.5
  ScaleType = 0
  ShowFrame = false
  X = -78.8252
  Y = -6.01719
FEATURE [TechDraw::DrawPage] Page
  KeepUpdated = true
  NextBalloonIndex = 1
  ProjectionType = 0
  Scale = 0.5
  Template = -> Template
  Views = -> [ProjGroup,Dimension,Dimension001,Dimension002,Dimension003,Dimension004,Dimension005,Dimension006,ProjGroup001,ProjGroup004,Dimension009,Dimension010,RichTextAnnotation,RichTextAnnotation001,RichTextAnnotation002,RichTextAnnotation003,RichTextAnnotation004]
